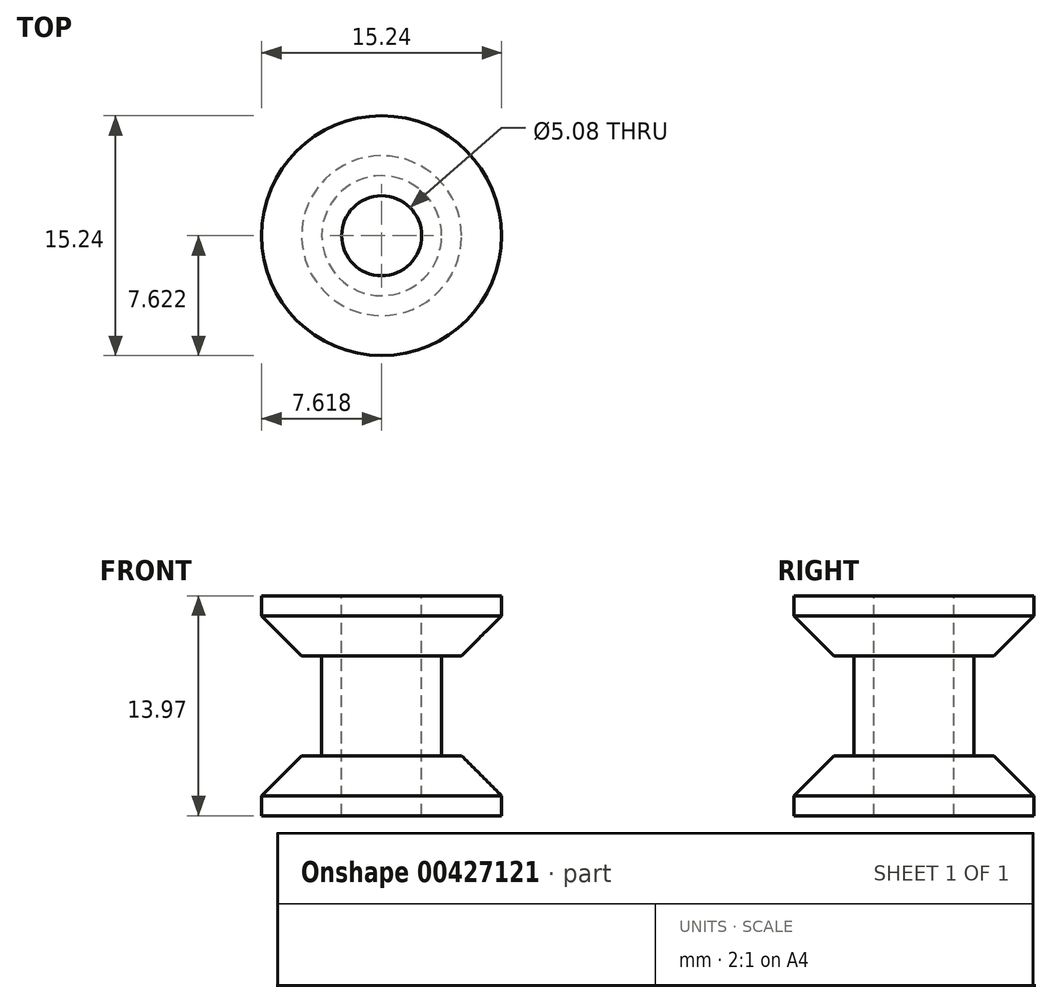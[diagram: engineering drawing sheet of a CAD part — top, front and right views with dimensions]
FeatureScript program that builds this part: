
annotation { "Feature Type Name" : "Feature", "Feature Type Description" : "" }
export const myFeature = defineFeature(function(context is Context, id is Id, definition is map)
    precondition{}
    {
        {
            var Q0;
            Q0=qCreatedBy(makeId("Top.planeOp"),FACE);
            var sketch = newSketch(context, id + "F0", { "sketchPlane" : qUnion([Q0])});
            skCircle(sketch, "E0", {"center": v(-5.84, 4.9) * mm, "radius": 7.62 * mm});
            skSolve(sketch);
        }
        {
            var Q0;
            Q0 = qSketchRegion(id + "F0", true);
            extrude(context, id + "F1", {"entities" : qUnion([Q0]), "depth" : 3.8 * mm});
        }
        {
            var Q0;
            Q0=makeQuery(id+"F1.opExtrude","CAP_FACE",FACE,{"disambiguationData":[OSD([sQuery(id+"F0.wireOp",EDGE,"E0")])],"isStart":false});
            var sketch = newSketch(context, id + "F2", { "sketchPlane" : qUnion([Q0])});
            skCircle(sketch, "E1", {"center": v(-5.84, 4.9) * mm, "radius": 3.81 * mm});
            skSolve(sketch);
        }
        {
            var Q0;
            Q0=makeQuery(id+"F2.imprint","IMPRINT",FACE,{"disambiguationData":[TD([[makeQuery(id+"F2.imprint","IMPRINT",EDGE,{"derivedFrom":sQuery(id+"F2.wireOp",EDGE,"E1")}),1.0]])]});
            extrude(context, id + "F3", {"entities" : qUnion([Q0]), "operationType" : NewBodyOperationType.ADD, "depth" : 6.35 * mm});
        }
        {
            var Q0;
            Q0=makeQuery(id+"F3.opExtrude","CAP_FACE",FACE,{"disambiguationData":[OSD([sQuery(id+"F2.wireOp",EDGE,"E1")])],"isStart":false});
            var sketch = newSketch(context, id + "F4", { "sketchPlane" : qUnion([Q0])});
            skCircle(sketch, "E2", {"center": v(-5.84, 4.9) * mm, "radius": 7.62 * mm});
            skSolve(sketch);
        }
        {
            var Q0;
            Q0 = qSketchRegion(id + "F4", true);
            extrude(context, id + "F5", {"entities" : qUnion([Q0]), "operationType" : NewBodyOperationType.ADD, "depth" : 3.8 * mm});
        }
        {
            var Q0;
            Q0=makeQuery(id+"F5.opExtrude","CAP_FACE",FACE,{"disambiguationData":[OSD([sQuery(id+"F4.wireOp",EDGE,"E2")])],"isStart":false});
            var sketch = newSketch(context, id + "F6", { "sketchPlane" : qUnion([Q0])});
            skPoint(sketch, "E3", {"position": v(-5.84, 4.9) * mm});
            skSolve(sketch);
        }
        {
            var Q0;
            Q0=sQuery(id+"F6.wireOp",VERTEX,"E3");
            var Q1;
            Q1=makeQuery(id+"F1.opExtrude","SWEPT_BODY",BODY,{"disambiguationData":[OSD([sQuery(id+"F0.wireOp",EDGE,"E0")])]});
            hole(context, id + "F7", {"style" : HoleStyle.SIMPLE, "endStyle" : HoleEndStyle.THROUGH, "holeDiameter" : 5.08 * mm, "isTappedThrough" : true, "tappedDepth" : 12.7 * mm, "tapClearance" : 3, "locations" : qUnion([Q0]), "scope" : qUnion([Q1])});
        }
        {
            var Q0;
            Q0=makeQuery(id+"F5.opExtrude","CAP_EDGE",EDGE,{"disambiguationData":[OSD([sQuery(id+"F4.wireOp",EDGE,"E2")])],"isStart":true});
            var Q1;
            Q1=makeQuery(id+"F1.opExtrude","CAP_EDGE",EDGE,{"disambiguationData":[OSD([sQuery(id+"F0.wireOp",EDGE,"E0")])],"isStart":false});
            chamfer(context, id + "F8", {"entities" : qUnion([Q0, Q1]), "width" : 2.54 * mm, "tangentPropagation" : true});
        }
    });
